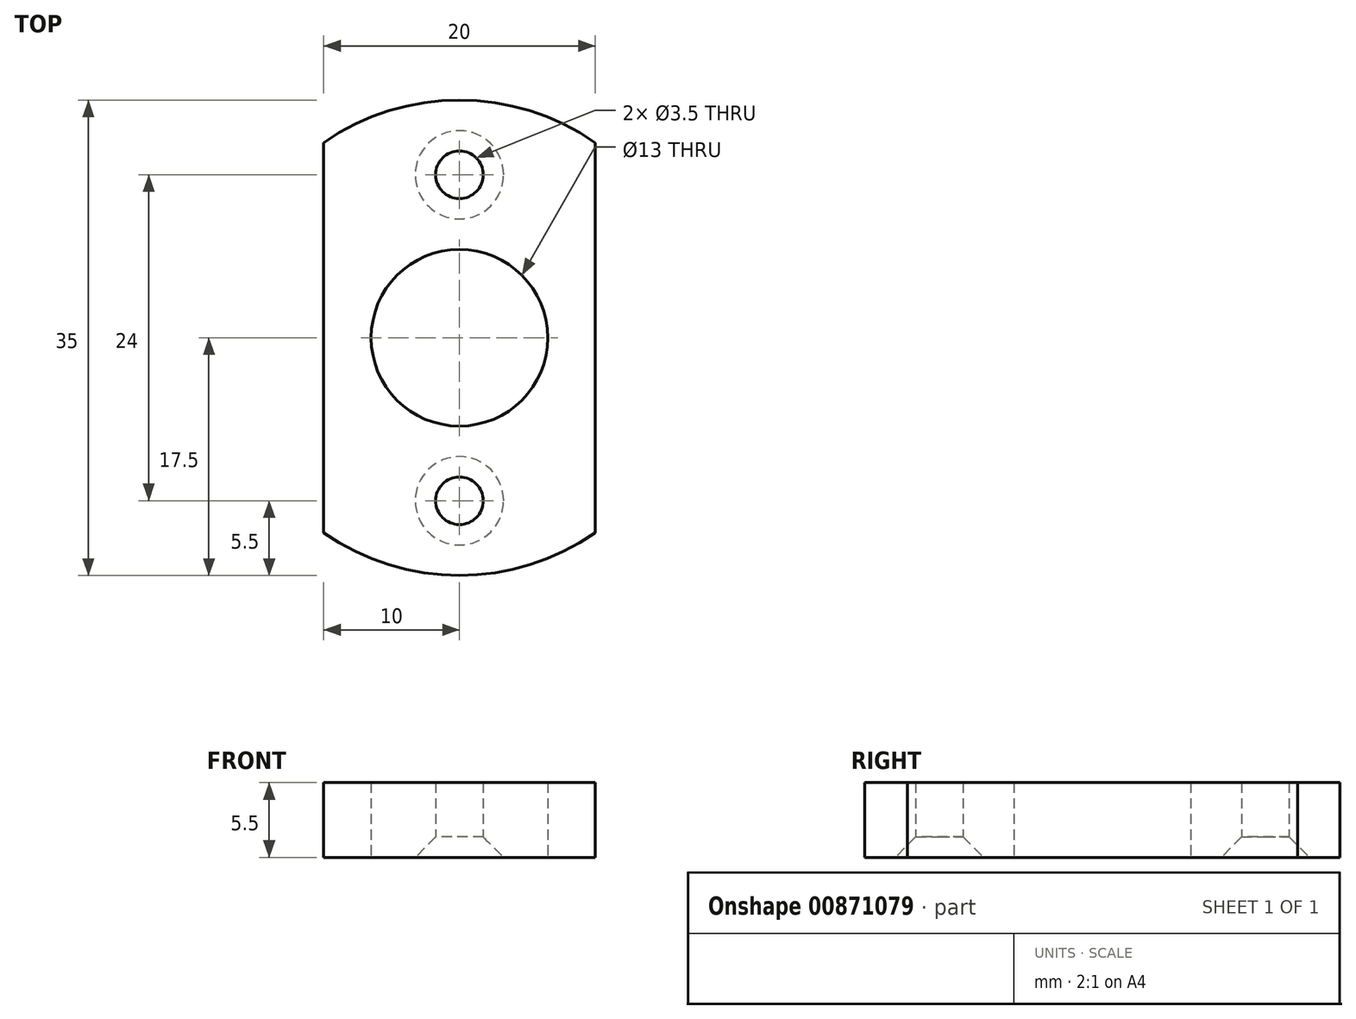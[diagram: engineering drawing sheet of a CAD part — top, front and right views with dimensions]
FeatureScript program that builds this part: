
annotation { "Feature Type Name" : "Feature", "Feature Type Description" : "" }
export const myFeature = defineFeature(function(context is Context, id is Id, definition is map)
    precondition{}
    {
        {
            var Q0;
            Q0=qCreatedBy(makeId("Top.planeOp"),FACE);
            var sketch = newSketch(context, id + "F0", { "sketchPlane" : qUnion([Q0])});
            skCircle(sketch, "E0", {"center": v(0, 0) * mm, "radius": 17.5 * mm});
            skLineSegment(sketch, "E1", {"start": v(0, 0) * mm, "end": v(10, 0) * mm});
            skLineSegment(sketch, "E2", {"start": v(10, 0) * mm, "end": v(10, 14.36) * mm});
            skLineSegment(sketch, "E3", {"start": v(10, 14.36) * mm, "end": v(10, -14.36) * mm});
            skLineSegment(sketch, "E4", {"start": v(0, 0) * mm, "end": v(-10, 0) * mm});
            skLineSegment(sketch, "E5", {"start": v(-10, 0) * mm, "end": v(-10, 14.36) * mm});
            skLineSegment(sketch, "E6", {"start": v(-10, 14.36) * mm, "end": v(-10, -14.36) * mm});
            skCircle(sketch, "E7", {"center": v(0, 0) * mm, "radius": 6.5 * mm});
            skLineSegment(sketch, "E8", {"start": v(0, 0) * mm, "end": v(0, 12) * mm});
            skLineSegment(sketch, "E9", {"start": v(0, 12) * mm, "end": v(0, -12) * mm});
            skCircle(sketch, "E10", {"center": v(0, -12) * mm, "radius": 1.75 * mm});
            skCircle(sketch, "E11", {"center": v(0, 12) * mm, "radius": 1.75 * mm});
            skSolve(sketch);
        }
        {
            var Q0;
            Q0=makeQuery(id+"F0.imprint","IMPRINT",FACE,{"disambiguationData":[TD([[makeQuery(id+"F0.imprint","IMPRINT",EDGE,{"derivedFrom":sQuery(id+"F0.wireOp",EDGE,"E11")}),-1.0]])]});
            var Q1;
            Q1=makeQuery(id+"F0.imprint","IMPRINT",FACE,{"disambiguationData":[TD([[makeQuery(id+"F0.imprint","IMPRINT",EDGE,{"derivedFrom":sQuery(id+"F0.wireOp",EDGE,"E10")}),-1.0]])]});
            extrude(context, id + "F1", {"entities" : qUnion([Q0, Q1]), "depth" : 5.5 * mm, "offsetDistance" : 25 * mm});
        }
        {
            var Q0;
            Q0=makeQuery(id+"F1.opExtrude","CAP_EDGE",EDGE,{"disambiguationData":[OSD([sQuery(id+"F0.wireOp",EDGE,"E10")])],"isStart":true});
            var Q1;
            Q1=makeQuery(id+"F1.opExtrude","CAP_EDGE",EDGE,{"disambiguationData":[OSD([sQuery(id+"F0.wireOp",EDGE,"E11")])],"isStart":true});
            chamfer(context, id + "F2", {"entities" : qUnion([Q0, Q1]), "width" : 1.5 * mm, "tangentPropagation" : true});
        }
    });
